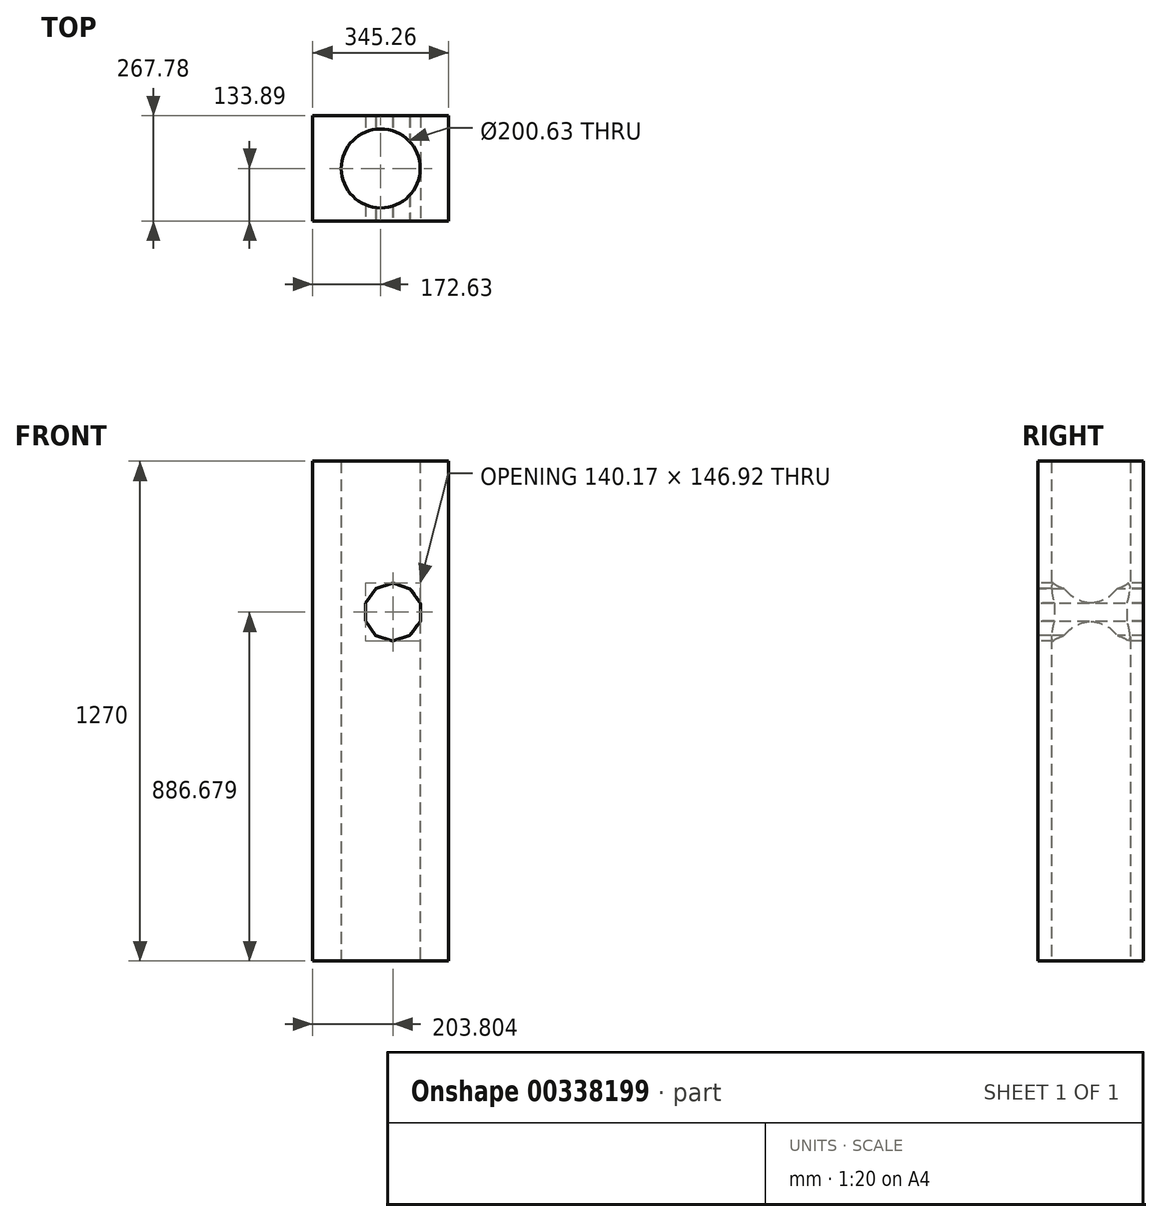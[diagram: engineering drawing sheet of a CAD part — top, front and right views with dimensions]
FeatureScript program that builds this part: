
annotation { "Feature Type Name" : "Feature", "Feature Type Description" : "" }
export const myFeature = defineFeature(function(context is Context, id is Id, definition is map)
    precondition{}
    {
        {
            var Q0;
            Q0=qCreatedBy(makeId("Top.planeOp"),FACE);
            var sketch = newSketch(context, id + "F0", { "sketchPlane" : qUnion([Q0])});
            skLineSegment(sketch, "E0.bottom", {"start": v(172.63, 133.89) * mm, "end": v(-172.63, 133.89) * mm});
            skLineSegment(sketch, "E0.top", {"start": v(172.63, -133.89) * mm, "end": v(-172.63, -133.89) * mm});
            skLineSegment(sketch, "E0.left", {"start": v(172.63, 133.89) * mm, "end": v(172.63, -133.89) * mm});
            skLineSegment(sketch, "E0.right", {"start": v(-172.63, 133.89) * mm, "end": v(-172.63, -133.89) * mm});
            skPoint(sketch, "E0.middle", {"position": v(0, 0) * mm});
            skCircle(sketch, "E1", {"center": v(0, 0) * mm, "radius": 100.32 * mm});
            skSolve(sketch);
        }
        {
            var Q0;
            Q0 = qSketchRegion(id + "F0", true);
            extrude(context, id + "F1", {"entities" : qUnion([Q0]), "endBound" : BoundingType.SYMMETRIC, "depth" : 1270 * mm});
        }
        {
            var Q0;
            Q0=makeQuery(id+"F1.opExtrude","SWEPT_FACE",FACE,{"disambiguationData":[OSD([sQuery(id+"F0.wireOp",EDGE,"E0.top")])]});
            var sketch = newSketch(context, id + "F2", { "sketchPlane" : qUnion([Q0])});
            skCircle(sketch, "E2.cCircle", {"center": v(31.17, 251.68) * mm, "radius": 69.87 * mm, "construction": true});
            skLineSegment(sketch, "E2.0", {"start": v(-38.47, 275.06) * mm, "end": v(-11.42, 311.53) * mm});
            skLineSegment(sketch, "E2.1", {"start": v(-11.42, 311.53) * mm, "end": v(31.9, 325.14) * mm});
            skLineSegment(sketch, "E2.2", {"start": v(31.9, 325.14) * mm, "end": v(74.94, 310.69) * mm});
            skLineSegment(sketch, "E2.3", {"start": v(74.94, 310.69) * mm, "end": v(101.26, 273.7) * mm});
            skLineSegment(sketch, "E2.4", {"start": v(101.26, 273.7) * mm, "end": v(100.82, 228.3) * mm});
            skLineSegment(sketch, "E2.5", {"start": v(100.82, 228.3) * mm, "end": v(73.77, 191.83) * mm});
            skLineSegment(sketch, "E2.6", {"start": v(73.77, 191.83) * mm, "end": v(30.45, 178.22) * mm});
            skLineSegment(sketch, "E2.7", {"start": v(30.45, 178.22) * mm, "end": v(-12.59, 192.67) * mm});
            skLineSegment(sketch, "E2.8", {"start": v(-12.59, 192.67) * mm, "end": v(-38.91, 229.66) * mm});
            skLineSegment(sketch, "E2.9", {"start": v(-38.91, 229.66) * mm, "end": v(-38.47, 275.06) * mm});
            skPoint(sketch, "E2.0.midPoint", {"position": v(-24.94, 293.3) * mm});
            skSolve(sketch);
        }
        {
            var Q0;
            Q0=makeQuery(id+"F2.imprint","IMPRINT",FACE,{"disambiguationData":[TD([[makeQuery(id+"F2.imprint","IMPRINT",EDGE,{"derivedFrom":sQuery(id+"F2.wireOp",EDGE,"E2.0")}),-1.0]])]});
            extrude(context, id + "F3", {"entities" : qUnion([Q0]), "operationType" : NewBodyOperationType.REMOVE, "oppositeDirection" : true, "depth" : 381 * mm});
        }
    });
